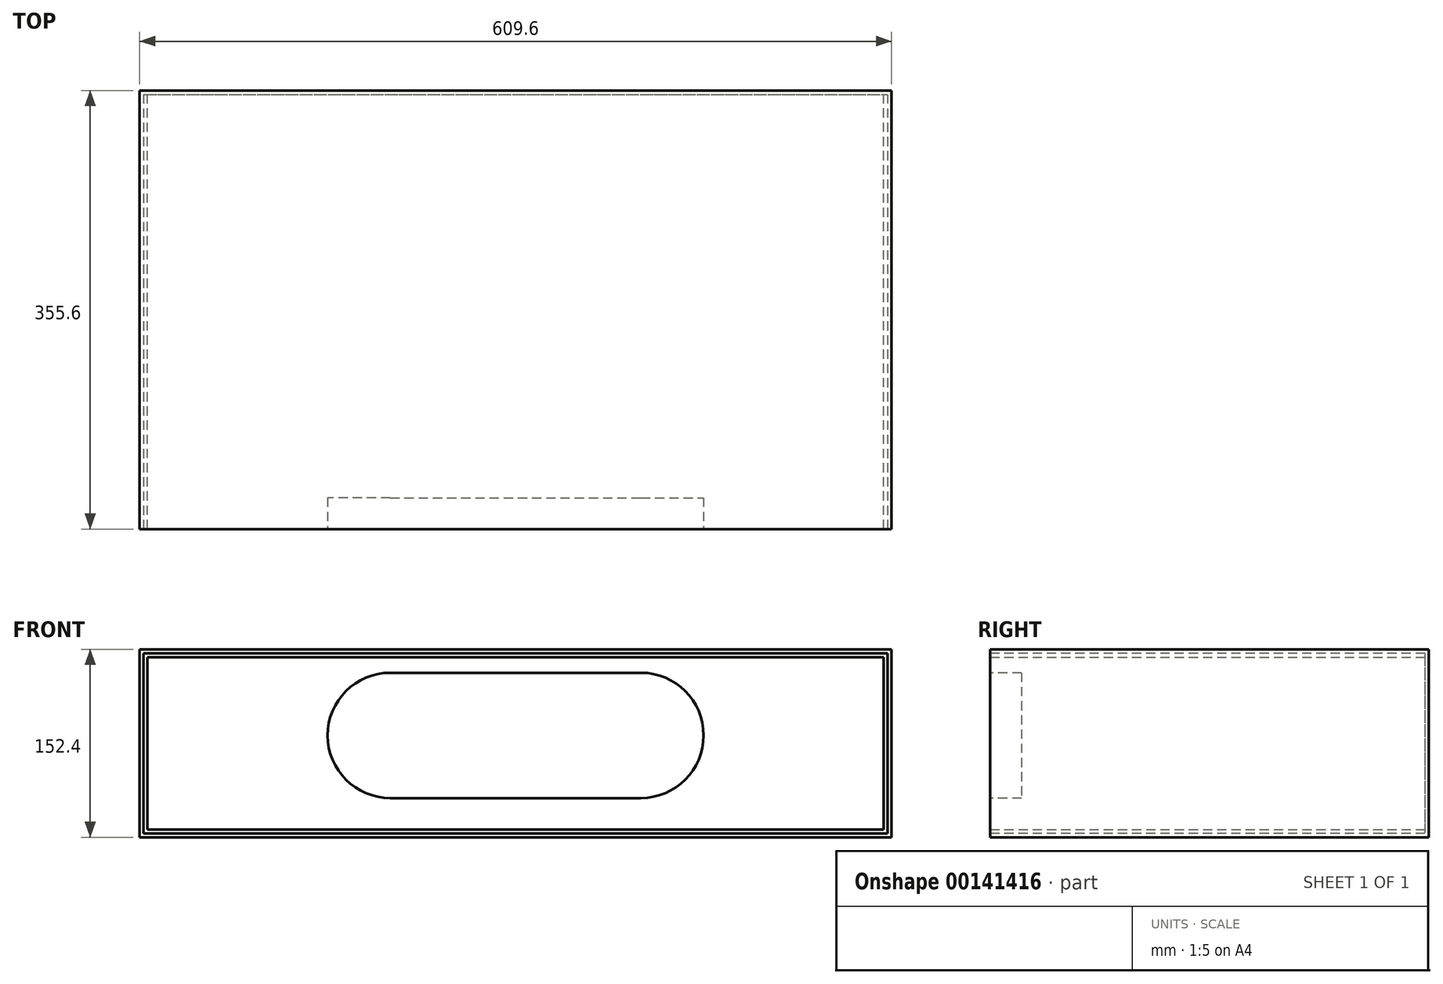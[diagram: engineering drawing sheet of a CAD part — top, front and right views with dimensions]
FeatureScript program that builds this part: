
annotation { "Feature Type Name" : "Feature", "Feature Type Description" : "" }
export const myFeature = defineFeature(function(context is Context, id is Id, definition is map)
    precondition{}
    {
        {
            var Q0;
            Q0=qCreatedBy(makeId("Front.planeOp"),FACE);
            var sketch = newSketch(context, id + "F0", { "sketchPlane" : qUnion([Q0])});
            skLineSegment(sketch, "E0.bottom", {"start": v(-304.8, 76.2) * mm, "end": v(304.8, 76.2) * mm});
            skLineSegment(sketch, "E0.top", {"start": v(-304.8, -76.2) * mm, "end": v(304.8, -76.2) * mm});
            skLineSegment(sketch, "E0.left", {"start": v(-304.8, 76.2) * mm, "end": v(-304.8, -76.2) * mm});
            skLineSegment(sketch, "E0.right", {"start": v(304.8, 76.2) * mm, "end": v(304.8, -76.2) * mm});
            skPoint(sketch, "E0.middle", {"position": v(0, 0) * mm});
            skSolve(sketch);
        }
        {
            var Q0;
            Q0 = qSketchRegion(id + "F0", true);
            extrude(context, id + "F1", {"entities" : qUnion([Q0]), "depth" : 355.6 * mm});
        }
        {
            var Q0;
            Q0=makeQuery(id+"F1.opExtrude","CAP_FACE",FACE,{"disambiguationData":[OSD([sQuery(id+"F0.wireOp",EDGE,"E0.bottom"),sQuery(id+"F0.wireOp",EDGE,"E0.top"),sQuery(id+"F0.wireOp",EDGE,"E0.left"),sQuery(id+"F0.wireOp",EDGE,"E0.right")])],"isStart":false});
            var sketch = newSketch(context, id + "F2", { "sketchPlane" : qUnion([Q0])});
            skLineSegment(sketch, "E1.bottom", {"start": v(-301.63, 73.02) * mm, "end": v(301.63, 73.02) * mm});
            skLineSegment(sketch, "E1.top", {"start": v(-301.63, -73.02) * mm, "end": v(301.63, -73.02) * mm});
            skLineSegment(sketch, "E1.left", {"start": v(-301.63, 73.02) * mm, "end": v(-301.63, -73.03) * mm});
            skLineSegment(sketch, "E1.right", {"start": v(301.63, 73.02) * mm, "end": v(301.63, -73.02) * mm});
            skSolve(sketch);
        }
        {
            var Q0;
            Q0 = qSketchRegion(id + "F2", true);
            extrude(context, id + "F3", {"entities" : qUnion([Q0]), "operationType" : NewBodyOperationType.REMOVE, "oppositeDirection" : true, "depth" : 352.42 * mm});
        }
        {
            var Q0;
            Q0=makeQuery(id+"F3.boolean.opBoolean","COPY",FACE,{"derivedFrom":makeQuery(id+"F3.opExtrude","CAP_FACE",FACE,{"disambiguationData":[OSD([sQuery(id+"F2.wireOp",EDGE,"E1.bottom"),sQuery(id+"F2.wireOp",EDGE,"E1.top"),sQuery(id+"F2.wireOp",EDGE,"E1.left"),sQuery(id+"F2.wireOp",EDGE,"E1.right")])],"isStart":false})});
            var sketch = newSketch(context, id + "F4", { "sketchPlane" : qUnion([Q0])});
            skLineSegment(sketch, "E2.bottom", {"start": v(-298.45, 69.85) * mm, "end": v(298.45, 69.85) * mm});
            skLineSegment(sketch, "E2.top", {"start": v(-298.45, -69.85) * mm, "end": v(298.45, -69.85) * mm});
            skLineSegment(sketch, "E2.left", {"start": v(-298.45, 69.85) * mm, "end": v(-298.45, -69.85) * mm});
            skLineSegment(sketch, "E2.right", {"start": v(298.45, 69.85) * mm, "end": v(298.45, -69.85) * mm});
            skSolve(sketch);
        }
        {
            var Q0;
            Q0 = qSketchRegion(id + "F4", true);
            var Q1;
            Q1=makeQuery(id+"F1.opExtrude","CAP_FACE",FACE,{"disambiguationData":[OSD([sQuery(id+"F0.wireOp",EDGE,"E0.bottom"),sQuery(id+"F0.wireOp",EDGE,"E0.top"),sQuery(id+"F0.wireOp",EDGE,"E0.left"),sQuery(id+"F0.wireOp",EDGE,"E0.right")])],"isStart":false});
            extrude(context, id + "F5", {"entities" : qUnion([Q0]), "operationType" : NewBodyOperationType.ADD, "endBound" : BoundingType.UP_TO_SURFACE, "endBoundEntityFace" : qUnion([Q1]), "depth" : 25.4 * mm});
        }
        {
            var Q0;
            Q0=makeQuery(id+"F5.opExtrude","CAP_FACE",FACE,{"disambiguationData":[OSD([sQuery(id+"F4.wireOp",EDGE,"E2.bottom"),sQuery(id+"F4.wireOp",EDGE,"E2.top"),sQuery(id+"F4.wireOp",EDGE,"E2.left"),sQuery(id+"F4.wireOp",EDGE,"E2.right")])],"isStart":false});
            var sketch = newSketch(context, id + "F6", { "sketchPlane" : qUnion([Q0])});
            skLineSegment(sketch, "E3", {"start": v(-101.6, -44.45) * mm, "end": v(101.6, -44.45) * mm});
            skLineSegment(sketch, "E4", {"start": v(-101.6, 57.15) * mm, "end": v(101.6, 57.15) * mm});
            skArc(sketch, "E5", {"start": v(-101.6, 57.15) * mm, "mid": v(-152.4, 6.35) * mm, "end": v(-101.6, -44.45) * mm});
            skArc(sketch, "E6", {"start": v(101.6, -44.45) * mm, "mid": v(152.4, 6.35) * mm, "end": v(101.6, 57.15) * mm});
            skLineSegment(sketch, "E7", {"start": v(0, 69.85) * mm, "end": v(0, -69.85) * mm});
            skSolve(sketch);
        }
        {
            var Q0;
            Q0 = qSketchRegion(id + "F6", true);
            extrude(context, id + "F7", {"entities" : qUnion([Q0]), "operationType" : NewBodyOperationType.REMOVE, "oppositeDirection" : true, "depth" : 25.4 * mm});
        }
    });
